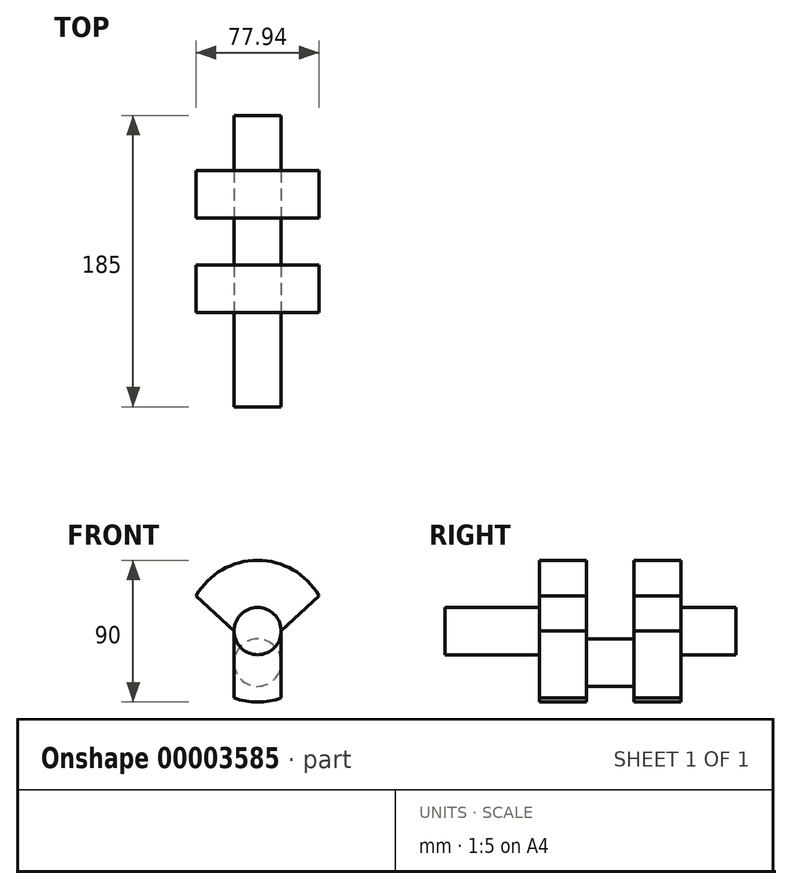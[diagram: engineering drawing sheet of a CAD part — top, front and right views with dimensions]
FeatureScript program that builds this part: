
annotation { "Feature Type Name" : "Feature", "Feature Type Description" : "" }
export const myFeature = defineFeature(function(context is Context, id is Id, definition is map)
    precondition{}
    {
        {
            var Q0;
            Q0=qCreatedBy(makeId("Right.planeOp"),FACE);
            var sketch = newSketch(context, id + "F0", { "sketchPlane" : qUnion([Q0])});
            skLineSegment(sketch, "E0", {"start": v(-61.26, 0) * mm, "end": v(28.74, 0) * mm});
            skLineSegment(sketch, "E1", {"start": v(-61.26, 0) * mm, "end": v(-61.26, 15) * mm});
            skLineSegment(sketch, "E2", {"start": v(123.74, 15) * mm, "end": v(123.74, 0) * mm});
            skLineSegment(sketch, "E3", {"start": v(28.74, 15) * mm, "end": v(28.74, -20) * mm});
            skLineSegment(sketch, "E4", {"start": v(28.74, -30) * mm, "end": v(-1.26, -30) * mm});
            skLineSegment(sketch, "E5", {"start": v(-1.26, -30) * mm, "end": v(-1.26, 15) * mm});
            skLineSegment(sketch, "E6", {"start": v(58.74, 15) * mm, "end": v(58.74, -20) * mm});
            skLineSegment(sketch, "E7", {"start": v(58.74, -30) * mm, "end": v(88.74, -30) * mm});
            skLineSegment(sketch, "E8", {"start": v(88.74, -30) * mm, "end": v(88.74, 15) * mm});
            skLineSegment(sketch, "E9.trimOffspring", {"start": v(58.74, 0) * mm, "end": v(123.74, 0) * mm});
            skLineSegment(sketch, "E10", {"start": v(28.74, -20) * mm, "end": v(58.74, -20) * mm});
            skLineSegment(sketch, "E11", {"start": v(28.74, -5) * mm, "end": v(58.74, -5) * mm});
            skLineSegment(sketch, "E12", {"start": v(-61.26, 15) * mm, "end": v(28.74, 15) * mm});
            skPoint(sketch, "E13.orphan", {"position": v(-61.26, 30) * mm});
            skPoint(sketch, "E14.orphan", {"position": v(123.74, 30) * mm});
            skLineSegment(sketch, "E15.trimOffspring", {"start": v(58.74, 15) * mm, "end": v(123.74, 15) * mm});
            skLineSegment(sketch, "E16", {"start": v(58.74, -30) * mm, "end": v(58.74, -20) * mm});
            skLineSegment(sketch, "E17", {"start": v(28.74, -30) * mm, "end": v(28.74, -20) * mm});
            skSolve(sketch);
        }
        {
            var Q0;
            {var subQ3=sQuery(id+"F0.wireOp",EDGE,"E1");Q0=makeQuery(id+"F0.imprint","IMPRINT",FACE,{"disambiguationData":[TD([[makeQuery(id+"F0.imprint","IMPRINT",EDGE,{"derivedFrom":subQ3}),-1.0]])]});}
            var Q1;
            {var subQ3=sQuery(id+"F0.wireOp",EDGE,"E3");var subQ5=sQuery(id+"F0.wireOp",EDGE,"E0");var subQ7=makeQuery(id+"F0.imprint","INTERSECT",VERTEX,{"derivedFrom":[subQ5,subQ3]});Q1=makeQuery(id+"F0.imprint","IMPRINT",FACE,{"disambiguationData":[TD([[makeQuery(id+"F0.imprint","IMPRINT",EDGE,{"disambiguationData":[TD([[subQ7,1.0]])],"derivedFrom":subQ5}),1.0]])]});}
            var Q2;
            {var subQ0=sQuery(id+"F0.wireOp",EDGE,"E15.trimOffspring");var subQ3=sQuery(id+"F0.wireOp",EDGE,"E6");var subQ4=makeQuery(id+"F0.imprint","INTERSECT",VERTEX,{"derivedFrom":[subQ3,subQ0]});Q2=makeQuery(id+"F0.imprint","IMPRINT",FACE,{"disambiguationData":[TD([[makeQuery(id+"F0.imprint","IMPRINT",EDGE,{"disambiguationData":[TD([[subQ4,-1.0]])],"derivedFrom":subQ3}),1.0]])]});}
            var Q3;
            {var subQ3=sQuery(id+"F0.wireOp",EDGE,"E2");Q3=makeQuery(id+"F0.imprint","IMPRINT",FACE,{"disambiguationData":[TD([[makeQuery(id+"F0.imprint","IMPRINT",EDGE,{"derivedFrom":subQ3}),-1.0]])]});}
            var Q4;
            {var subQ5=sQuery(id+"F0.wireOp",EDGE,"E7");Q4=makeQuery(id+"F0.imprint","IMPRINT",FACE,{"disambiguationData":[TD([[makeQuery(id+"F0.imprint","IMPRINT",EDGE,{"derivedFrom":subQ5}),1.0]])]});}
            var Q5;
            {var subQ3=sQuery(id+"F0.wireOp",EDGE,"E4");Q5=makeQuery(id+"F0.imprint","IMPRINT",FACE,{"disambiguationData":[TD([[makeQuery(id+"F0.imprint","IMPRINT",EDGE,{"derivedFrom":subQ3}),-1.0]])]});}
            var Q6;
            Q6=sQuery(id+"F0.wireOp",EDGE,"E12");
            revolve(context, id + "F1", {"entities" : qUnion([Q0, Q1, Q2, Q3, Q4, Q5]), "axis" : qUnion([Q6]), "revolveType" : RevolveType.FULL});
        }
        {
            var Q0;
            {var subQ1=sQuery(id+"F0.wireOp",EDGE,"E10");Q0=makeQuery(id+"F0.imprint","IMPRINT",FACE,{"disambiguationData":[TD([[makeQuery(id+"F0.imprint","IMPRINT",EDGE,{"derivedFrom":subQ1}),1.0]])]});}
            var Q1;
            Q1=sQuery(id+"F0.wireOp",EDGE,"E11");
            revolve(context, id + "F2", {"operationType" : NewBodyOperationType.ADD, "entities" : qUnion([Q0]), "axis" : qUnion([Q1]), "revolveType" : RevolveType.FULL});
        }
        {
            var Q0;
            Q0=makeQuery(id+"F1.opRevolve","SWEPT_FACE",FACE,{"disambiguationData":[OSD([sQuery(id+"F0.wireOp",EDGE,"E5")])]});
            var sketch = newSketch(context, id + "F3", { "sketchPlane" : qUnion([Q0])});
            skLineSegment(sketch, "E18", {"start": v(15, 15) * mm, "end": v(15, -27.43) * mm});
            skLineSegment(sketch, "E19", {"start": v(-15, 15) * mm, "end": v(-15, -27.43) * mm});
            skArc(sketch, "E20", {"start": v(-38.97, 37.5) * mm, "mid": v(-59.45, -6.95) * mm, "end": v(-15, -27.43) * mm});
            skArc(sketch, "E21", {"start": v(15, -27.43) * mm, "mid": v(59.45, -6.95) * mm, "end": v(38.97, 37.5) * mm});
            skCircle(sketch, "E22", {"center": v(0, 15) * mm, "radius": 15 * mm});
            skLineSegment(sketch, "E23", {"start": v(15, 15) * mm, "end": v(38.97, 37.5) * mm});
            skLineSegment(sketch, "E24", {"start": v(-15, 15) * mm, "end": v(-38.97, 37.5) * mm});
            skSolve(sketch);
        }
        {
            var Q0;
            {var subQ1=sQuery(id+"F3.wireOp",EDGE,"E19");Q0=makeQuery(id+"F3.imprint","IMPRINT",FACE,{"disambiguationData":[TD([[makeQuery(id+"F3.imprint","IMPRINT",EDGE,{"derivedFrom":subQ1}),-1.0]])]});}
            var Q1;
            {var subQ1=sQuery(id+"F3.wireOp",EDGE,"E18");Q1=makeQuery(id+"F3.imprint","IMPRINT",FACE,{"disambiguationData":[TD([[makeQuery(id+"F3.imprint","IMPRINT",EDGE,{"derivedFrom":subQ1}),1.0]])]});}
            extrude(context, id + "F4", {"entities" : qUnion([Q0, Q1]), "operationType" : NewBodyOperationType.REMOVE, "endBound" : BoundingType.THROUGH_ALL, "oppositeDirection" : true, "depth" : 50 * mm});
        }
    });
